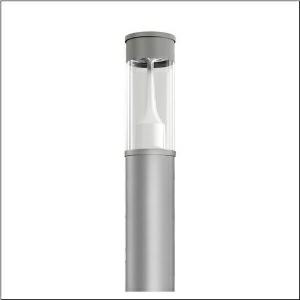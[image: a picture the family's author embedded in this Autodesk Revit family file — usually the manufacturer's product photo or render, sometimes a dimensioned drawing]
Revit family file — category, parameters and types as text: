
# Revit family: city-light_400_iq___st1_2a_5xa5305mf14hp_fa50
name_source: partatom
category: Lighting Fixtures
units: mm (PartAtom-declared; Revit-internal decimal feet)

## family parameters
Cut with Voids When Loaded = No
Host = Face
Light Source = No
Part Type = Normal
Room Calculation Point = No
Round Connector Dimension = Use Diameter
Shared = No

## types (1)
- --- (1 x LED, 4240 lm, 33.6 W, 2700K)
    Apparent Load = 34 VA
    CIE Flux Codes = 22 61 94 96 100
    Color Rendering = 70
    Color Temperature = 2700K
    Default Elevation = 1800 mm
    Description = City-Light 400 iQ, light pillar, Module 540 iQ-SR, primary light control with 3 zone facetted reflector, of plastic, silver coated, highly specular, structured, primary optical cover: cover, of PMMA, transparent, partly coated, light distribution: ST1.2a, primary light characteristic: asymmetric, LED, High Power LED, rated luminous flux: 4.240lm, luminous efficacy: 126lm/W, light colour: 727, colour temperature: 2700K, control gear: iQ Street-Remote, control: pre-setting: logarithmic dimming characteristic, Street-Remote, Auto-Match, Temp-Guard, Lumen-Switch, Night-Set, Smart-Wire, Light-Fading, Desk-Remote (wireless, voltage-free reading and setting of iQ features in the workshop via application-optimized NFC function/RFID function), optimised constant luminous flux control (CLO 2.0), with terminal, 6-pole, max. 2.5mm², mains connection: 230..240V, AC, 50/60Hz, start of lifetime: 34W, end of service life: 36W, reduction: 15W, luminaire housing, cylindrical, of extruded aluminium section, coated, Siteco® metallic grey (DB 702S), length: 4.694mm, diameter: 200mm, Module 540 iQ-SR, traffic white (RAL 9016), equipment: Power, protection rating (complete): IP65, insulation class (complete): insulation class II (safety insulation), certification: CE, ENEC, VDE, packaging unit: 1 piece

Light Distribution: ST1.2a
    Height = 500 mm
    Lamp = 1 x LED
    Lamp Light Flux = 4240 lm
    Lamp Power = 33.6 W
    Lamp count = 1
    Length = 200 mm  [stored 0.656168 ft]
    Luminous efficacy = 126 lm/W
    Manufacturer = Siteco
    ModVariant = No
    Model = 5XA5305MF14HP
    Mounting Place = Floor
    Mounting Type = Freestanding
    Number of Poles = 1
    OnlyDefault = Yes
    Power Factor = 1
    Product Name = City-Light 400 iQ | ST1.2a
    Product group = light pillar
    ProductGroupID = 1301
    Protection Class = Protection class II
    Protection Degree = IP 65
    RLX_Detail_Level = 1
    RLX_Emergency_Light_Flux = 0 lm
    RLX_Emergency_Type = 0
    RLX_Emergency_Type_DB = No
    RlxData = <blob elided: 53705 chars, md5=6adee34e>
    Socket = socket
    Standby Power = 0 W
    System Light Flux = 4240 lm
    System Power = 34 W
    Type Comments = factory setting: luminous flux: 100 % | dim-lin: 254 | 695 mA
    Type Image = l_1006916.jpg
    URL = http://relux.com
    VarID = @adj_173983
    Voltage = 0 V
    Weight = 0.00 kg
    Width = 0 mm  [stored 0 ft]

note: [stored X ft] marks values corroborated as IEEE doubles in the binary element streams (Revit-internal decimal feet)

## geometry (parser evidence)
native form markers: Blend x4, Sweep x12
no freeform markers — native parametric forms only
